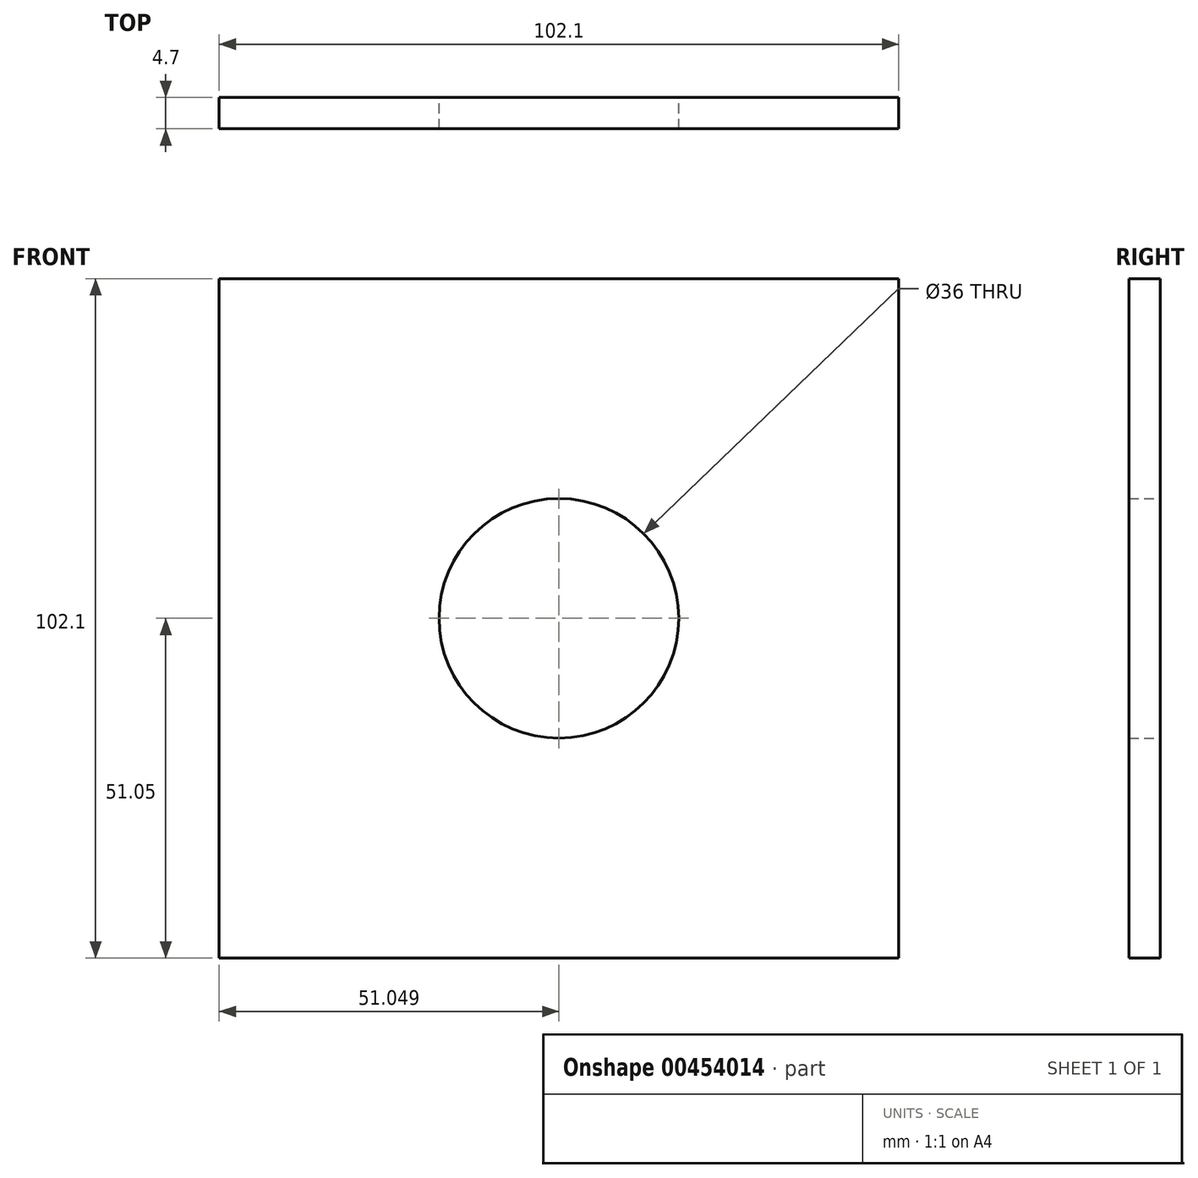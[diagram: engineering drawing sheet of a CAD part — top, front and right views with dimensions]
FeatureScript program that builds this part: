
annotation { "Feature Type Name" : "Feature", "Feature Type Description" : "" }
export const myFeature = defineFeature(function(context is Context, id is Id, definition is map)
    precondition{}
    {
        {
            var Q0;
            Q0=qCreatedBy(makeId("Front.planeOp"),FACE);
            var sketch = newSketch(context, id + "F0", { "sketchPlane" : qUnion([Q0])});
            skLineSegment(sketch, "E0.bottom", {"start": v(-57.58, 37.07) * mm, "end": v(44.52, 37.07) * mm});
            skLineSegment(sketch, "E0.top", {"start": v(-57.58, -65.03) * mm, "end": v(44.52, -65.03) * mm});
            skLineSegment(sketch, "E0.left", {"start": v(-57.58, 37.07) * mm, "end": v(-57.58, -65.03) * mm});
            skLineSegment(sketch, "E0.right", {"start": v(44.52, 37.07) * mm, "end": v(44.52, -65.03) * mm});
            skCircle(sketch, "E1", {"center": v(-6.53, -13.98) * mm, "radius": 18 * mm});
            skPoint(sketch, "E2.positionSnap0", {"position": v(-6.53, 37.07) * mm});
            skPoint(sketch, "E2.positionSnap1", {"position": v(44.52, -13.98) * mm});
            skSolve(sketch);
        }
        {
            var Q0;
            Q0=makeQuery(id+"F0.imprint","IMPRINT",FACE,{"disambiguationData":[TD([[makeQuery(id+"F0.imprint","IMPRINT",EDGE,{"derivedFrom":sQuery(id+"F0.wireOp",EDGE,"E0.bottom")}),-1.0]])]});
            extrude(context, id + "F1", {"entities" : qUnion([Q0]), "endBound" : BoundingType.SYMMETRIC, "depth" : 4.7 * mm});
        }
    });
